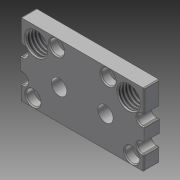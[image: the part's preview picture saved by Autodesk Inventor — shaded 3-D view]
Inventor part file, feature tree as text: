
AUTODESK INVENTOR PART (.ipt)
format: ipt  version: 2014 SP1 (Build 180222100, 222)  size: 250,368 bytes
history: native  units: in
note: dims shown in document units (in); Inventor stores cm internally (conversion verified against a paired STEP export)
features: thread x3, extrude x2, fillet x1, mirror x1
ambient origin geometry x8: Origin, YZ Plane, XZ Plane, XY Plane, X Axis, Y Axis, Z Axis, Center Point
bodies: Solid1 (feature_tree)
feature tree (7):
  extrude  "Extrusion1"  Depth=0.125in
  extrude  "Extrusion2"  Depth=1.75in
  fillet  "Fillet1"  Radius=0.05in
  thread  "Thread1"  [1 undecoded]
  thread  "Thread2"  [1 undecoded]
  thread  "Thread3"  [1 undecoded]
  mirror  "Mirror1"
note: 3 required parameter values undecoded (feature->parameter linkage not recoverable at this tier; creation-order binding heuristic only, values carry confidence <= 0.55)
